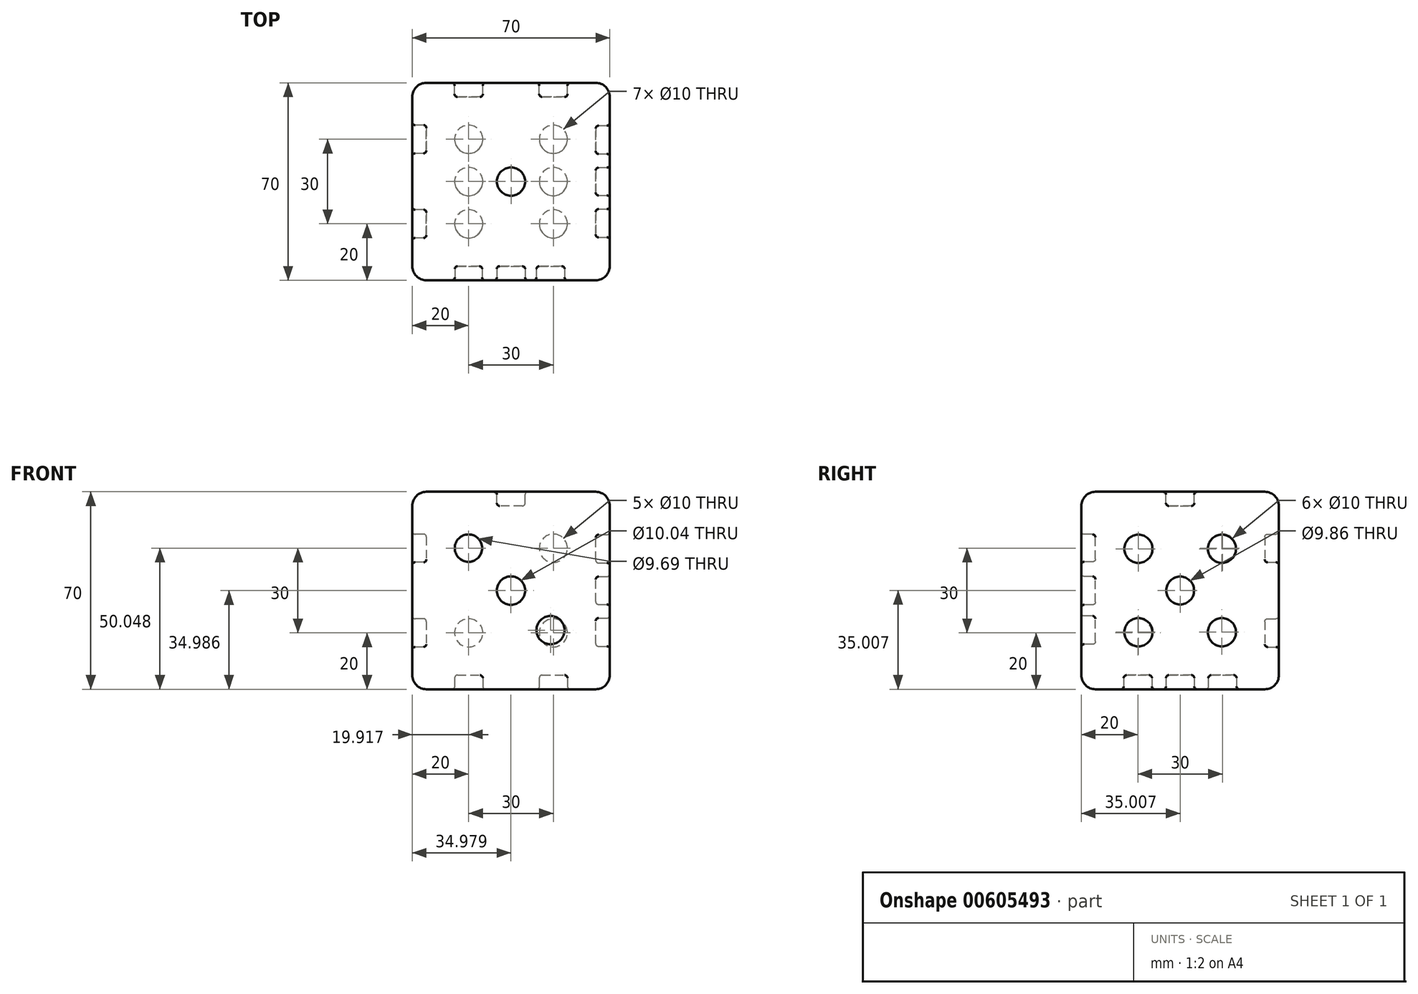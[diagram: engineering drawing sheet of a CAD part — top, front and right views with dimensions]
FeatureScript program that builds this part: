
annotation { "Feature Type Name" : "Feature", "Feature Type Description" : "" }
export const myFeature = defineFeature(function(context is Context, id is Id, definition is map)
    precondition{}
    {
        {
            var Q0;
            Q0=qCreatedBy(makeId("Top.planeOp"),FACE);
            var sketch = newSketch(context, id + "F0", { "sketchPlane" : qUnion([Q0])});
            skLineSegment(sketch, "E0.bottom", {"start": v(-35, -35) * mm, "end": v(35, -35) * mm});
            skLineSegment(sketch, "E0.top", {"start": v(-35, 35) * mm, "end": v(35, 35) * mm});
            skLineSegment(sketch, "E0.left", {"start": v(-35, -35) * mm, "end": v(-35, 35) * mm});
            skLineSegment(sketch, "E0.right", {"start": v(35, -35) * mm, "end": v(35, 35) * mm});
            skPoint(sketch, "E0.middle", {"position": v(0, 0) * mm});
            skSolve(sketch);
        }
        {
            var Q0;
            Q0=makeQuery(id+"F0.imprint","IMPRINT",FACE,{"disambiguationData":[TD([[makeQuery(id+"F0.imprint","IMPRINT",EDGE,{"derivedFrom":sQuery(id+"F0.wireOp",EDGE,"E0.bottom")}),1.0]])]});
            extrude(context, id + "F1", {"entities" : qUnion([Q0]), "depth" : 70 * mm, "offsetDistance" : 25 * mm});
        }
        {
            var Q0;
            Q0=makeQuery(id+"F1.opExtrude","SWEPT_EDGE",EDGE,{"disambiguationData":[OSD([sQuery(id+"F0.wireOp",EDGE,"E0.bottom"),sQuery(id+"F0.wireOp",EDGE,"E0.left")])]});
            var Q1;
            Q1=makeQuery(id+"F1.opExtrude","SWEPT_FACE",FACE,{"disambiguationData":[OSD([sQuery(id+"F0.wireOp",EDGE,"E0.bottom")])]});
            var Q2;
            Q2=makeQuery(id+"F1.opExtrude","SWEPT_EDGE",EDGE,{"disambiguationData":[OSD([sQuery(id+"F0.wireOp",EDGE,"E0.bottom"),sQuery(id+"F0.wireOp",EDGE,"E0.right")])]});
            var Q3;
            Q3=makeQuery(id+"F1.opExtrude","CAP_FACE",FACE,{"disambiguationData":[OSD([sQuery(id+"F0.wireOp",EDGE,"E0.bottom"),sQuery(id+"F0.wireOp",EDGE,"E0.top"),sQuery(id+"F0.wireOp",EDGE,"E0.left"),sQuery(id+"F0.wireOp",EDGE,"E0.right")])],"isStart":false});
            var Q4;
            Q4=makeQuery(id+"F1.opExtrude","SWEPT_EDGE",EDGE,{"disambiguationData":[OSD([sQuery(id+"F0.wireOp",EDGE,"E0.top"),sQuery(id+"F0.wireOp",EDGE,"E0.right")])]});
            var Q5;
            Q5=makeQuery(id+"F1.opExtrude","CAP_EDGE",EDGE,{"disambiguationData":[OSD([sQuery(id+"F0.wireOp",EDGE,"E0.bottom")])],"isStart":true});
            var Q6;
            Q6=makeQuery(id+"F1.opExtrude","SWEPT_FACE",FACE,{"disambiguationData":[OSD([sQuery(id+"F0.wireOp",EDGE,"E0.left")])]});
            var Q7;
            Q7=makeQuery(id+"F1.opExtrude","CAP_EDGE",EDGE,{"disambiguationData":[OSD([sQuery(id+"F0.wireOp",EDGE,"E0.bottom")])],"isStart":false});
            var Q8;
            Q8=makeQuery(id+"F1.opExtrude","SWEPT_FACE",FACE,{"disambiguationData":[OSD([sQuery(id+"F0.wireOp",EDGE,"E0.right")])]});
            var Q9;
            Q9=makeQuery(id+"F1.opExtrude","CAP_EDGE",EDGE,{"disambiguationData":[OSD([sQuery(id+"F0.wireOp",EDGE,"E0.top")])],"isStart":false});
            var Q10;
            Q10=makeQuery(id+"F1.opExtrude","CAP_EDGE",EDGE,{"disambiguationData":[OSD([sQuery(id+"F0.wireOp",EDGE,"E0.left")])],"isStart":false});
            var Q11;
            Q11=makeQuery(id+"F1.opExtrude","CAP_EDGE",EDGE,{"disambiguationData":[OSD([sQuery(id+"F0.wireOp",EDGE,"E0.right")])],"isStart":true});
            var Q12;
            Q12=makeQuery(id+"F1.opExtrude","CAP_EDGE",EDGE,{"disambiguationData":[OSD([sQuery(id+"F0.wireOp",EDGE,"E0.right")])],"isStart":false});
            var Q13;
            Q13=makeQuery(id+"F1.opExtrude","CAP_FACE",FACE,{"disambiguationData":[OSD([sQuery(id+"F0.wireOp",EDGE,"E0.bottom"),sQuery(id+"F0.wireOp",EDGE,"E0.top"),sQuery(id+"F0.wireOp",EDGE,"E0.left"),sQuery(id+"F0.wireOp",EDGE,"E0.right")])],"isStart":true});
            var Q14;
            Q14=makeQuery(id+"F1.opExtrude","SWEPT_EDGE",EDGE,{"disambiguationData":[OSD([sQuery(id+"F0.wireOp",EDGE,"E0.top"),sQuery(id+"F0.wireOp",EDGE,"E0.left")])]});
            var Q15;
            Q15=makeQuery(id+"F1.opExtrude","SWEPT_FACE",FACE,{"disambiguationData":[OSD([sQuery(id+"F0.wireOp",EDGE,"E0.top")])]});
            var Q16;
            Q16=makeQuery(id+"F1.opExtrude","CAP_EDGE",EDGE,{"disambiguationData":[OSD([sQuery(id+"F0.wireOp",EDGE,"E0.top")])],"isStart":true});
            var Q17;
            Q17=makeQuery(id+"F1.opExtrude","CAP_EDGE",EDGE,{"disambiguationData":[OSD([sQuery(id+"F0.wireOp",EDGE,"E0.left")])],"isStart":true});
            fillet(context, id + "F2", {"entities" : qUnion([Q0, Q1, Q2, Q3, Q4, Q5, Q6, Q7, Q8, Q9, Q10, Q11, Q12, Q13, Q14, Q15, Q16, Q17]), "radius" : 5 * mm, "tangentPropagation" : true, "allowEdgeOverflow" : false});
        }
        {
            var Q0;
            Q0=makeQuery(id+"F1.opExtrude","CAP_FACE",FACE,{"disambiguationData":[OSD([sQuery(id+"F0.wireOp",EDGE,"E0.bottom"),sQuery(id+"F0.wireOp",EDGE,"E0.top"),sQuery(id+"F0.wireOp",EDGE,"E0.left"),sQuery(id+"F0.wireOp",EDGE,"E0.right")])],"isStart":false});
            var sketch = newSketch(context, id + "F3", { "sketchPlane" : qUnion([Q0])});
            skCircle(sketch, "E1", {"center": v(0, 0) * mm, "radius": 5 * mm});
            skSolve(sketch);
        }
        {
            var Q0;
            Q0=makeQuery(id+"F3.imprint","IMPRINT",FACE,{"disambiguationData":[TD([[makeQuery(id+"F3.imprint","IMPRINT",EDGE,{"derivedFrom":sQuery(id+"F3.wireOp",EDGE,"E1")}),1.0]])]});
            extrude(context, id + "F4", {"entities" : qUnion([Q0]), "operationType" : NewBodyOperationType.REMOVE, "oppositeDirection" : true, "depth" : 5 * mm, "offsetDistance" : 25 * mm});
        }
        {
            var Q0;
            Q0=makeQuery(id+"F1.opExtrude","SWEPT_FACE",FACE,{"disambiguationData":[OSD([sQuery(id+"F0.wireOp",EDGE,"E0.bottom")])]});
            var sketch = newSketch(context, id + "F5", { "sketchPlane" : qUnion([Q0])});
            skCircle(sketch, "E2", {"center": v(-0.02, 34.99) * mm, "radius": 5.02 * mm});
            skCircle(sketch, "E3", {"center": v(-15.08, 50.05) * mm, "radius": 4.85 * mm});
            skCircle(sketch, "E4", {"center": v(14, 20.97) * mm, "radius": 5 * mm});
            skSolve(sketch);
        }
        {
            var Q0;
            Q0=makeQuery(id+"F5.imprint","IMPRINT",FACE,{"disambiguationData":[TD([[makeQuery(id+"F5.imprint","IMPRINT",EDGE,{"derivedFrom":sQuery(id+"F5.wireOp",EDGE,"E3")}),1.0]])]});
            var Q1;
            Q1=makeQuery(id+"F5.imprint","IMPRINT",FACE,{"disambiguationData":[TD([[makeQuery(id+"F5.imprint","IMPRINT",EDGE,{"derivedFrom":sQuery(id+"F5.wireOp",EDGE,"E2")}),1.0]])]});
            var Q2;
            Q2=makeQuery(id+"F5.imprint","IMPRINT",FACE,{"disambiguationData":[TD([[makeQuery(id+"F5.imprint","IMPRINT",EDGE,{"derivedFrom":sQuery(id+"F5.wireOp",EDGE,"E4")}),1.0]])]});
            extrude(context, id + "F6", {"entities" : qUnion([Q0, Q1, Q2]), "operationType" : NewBodyOperationType.REMOVE, "oppositeDirection" : true, "depth" : 5 * mm, "offsetDistance" : 25 * mm});
        }
        {
            var Q0;
            Q0=makeQuery(id+"F1.opExtrude","SWEPT_FACE",FACE,{"disambiguationData":[OSD([sQuery(id+"F0.wireOp",EDGE,"E0.top")])]});
            var sketch = newSketch(context, id + "F7", { "sketchPlane" : qUnion([Q0])});
            skCircle(sketch, "E5", {"center": v(-15, 50) * mm, "radius": 5 * mm});
            skCircle(sketch, "E6", {"center": v(-15, 20) * mm, "radius": 5 * mm});
            skCircle(sketch, "E7", {"center": v(15, 50) * mm, "radius": 5 * mm});
            skCircle(sketch, "E8", {"center": v(15, 20) * mm, "radius": 5 * mm});
            skSolve(sketch);
        }
        {
            var Q0;
            Q0=makeQuery(id+"F7.imprint","IMPRINT",FACE,{"disambiguationData":[TD([[makeQuery(id+"F7.imprint","IMPRINT",EDGE,{"derivedFrom":sQuery(id+"F7.wireOp",EDGE,"E7")}),1.0]])]});
            var Q1;
            Q1=makeQuery(id+"F7.imprint","IMPRINT",FACE,{"disambiguationData":[TD([[makeQuery(id+"F7.imprint","IMPRINT",EDGE,{"derivedFrom":sQuery(id+"F7.wireOp",EDGE,"E8")}),1.0]])]});
            var Q2;
            Q2=makeQuery(id+"F7.imprint","IMPRINT",FACE,{"disambiguationData":[TD([[makeQuery(id+"F7.imprint","IMPRINT",EDGE,{"derivedFrom":sQuery(id+"F7.wireOp",EDGE,"E5")}),1.0]])]});
            var Q3;
            Q3=makeQuery(id+"F7.imprint","IMPRINT",FACE,{"disambiguationData":[TD([[makeQuery(id+"F7.imprint","IMPRINT",EDGE,{"derivedFrom":sQuery(id+"F7.wireOp",EDGE,"E6")}),1.0]])]});
            extrude(context, id + "F8", {"entities" : qUnion([Q0, Q1, Q2, Q3]), "operationType" : NewBodyOperationType.REMOVE, "oppositeDirection" : true, "depth" : 5 * mm, "offsetDistance" : 25 * mm});
        }
        {
            var Q0;
            Q0=makeQuery(id+"F1.opExtrude","CAP_FACE",FACE,{"disambiguationData":[OSD([sQuery(id+"F0.wireOp",EDGE,"E0.bottom"),sQuery(id+"F0.wireOp",EDGE,"E0.top"),sQuery(id+"F0.wireOp",EDGE,"E0.left"),sQuery(id+"F0.wireOp",EDGE,"E0.right")])],"isStart":true});
            var sketch = newSketch(context, id + "F9", { "sketchPlane" : qUnion([Q0])});
            skCircle(sketch, "E9", {"center": v(-15, 0) * mm, "radius": 5 * mm});
            skCircle(sketch, "E10", {"center": v(15, 0) * mm, "radius": 5 * mm});
            skCircle(sketch, "E11", {"center": v(-15, 15) * mm, "radius": 5 * mm});
            skCircle(sketch, "E12", {"center": v(15, 15) * mm, "radius": 5 * mm});
            skCircle(sketch, "E13", {"center": v(15, -15) * mm, "radius": 5 * mm});
            skCircle(sketch, "E14", {"center": v(-15, -15) * mm, "radius": 5 * mm});
            skSolve(sketch);
        }
        {
            var Q0;
            Q0=makeQuery(id+"F9.imprint","IMPRINT",FACE,{"disambiguationData":[TD([[makeQuery(id+"F9.imprint","IMPRINT",EDGE,{"derivedFrom":sQuery(id+"F9.wireOp",EDGE,"E11")}),1.0]])]});
            var Q1;
            Q1=makeQuery(id+"F9.imprint","IMPRINT",FACE,{"disambiguationData":[TD([[makeQuery(id+"F9.imprint","IMPRINT",EDGE,{"derivedFrom":sQuery(id+"F9.wireOp",EDGE,"E10")}),1.0]])]});
            var Q2;
            Q2=makeQuery(id+"F9.imprint","IMPRINT",FACE,{"disambiguationData":[TD([[makeQuery(id+"F9.imprint","IMPRINT",EDGE,{"derivedFrom":sQuery(id+"F9.wireOp",EDGE,"E9")}),1.0]])]});
            var Q3;
            Q3=makeQuery(id+"F9.imprint","IMPRINT",FACE,{"disambiguationData":[TD([[makeQuery(id+"F9.imprint","IMPRINT",EDGE,{"derivedFrom":sQuery(id+"F9.wireOp",EDGE,"E14")}),1.0]])]});
            var Q4;
            Q4=makeQuery(id+"F9.imprint","IMPRINT",FACE,{"disambiguationData":[TD([[makeQuery(id+"F9.imprint","IMPRINT",EDGE,{"derivedFrom":sQuery(id+"F9.wireOp",EDGE,"E13")}),1.0]])]});
            var Q5;
            Q5=makeQuery(id+"F9.imprint","IMPRINT",FACE,{"disambiguationData":[TD([[makeQuery(id+"F9.imprint","IMPRINT",EDGE,{"derivedFrom":sQuery(id+"F9.wireOp",EDGE,"E12")}),1.0]])]});
            extrude(context, id + "F10", {"entities" : qUnion([Q0, Q1, Q2, Q3, Q4, Q5]), "operationType" : NewBodyOperationType.REMOVE, "oppositeDirection" : true, "depth" : 5 * mm, "offsetDistance" : 25 * mm});
        }
        {
            var Q0;
            Q0=makeQuery(id+"F1.opExtrude","SWEPT_FACE",FACE,{"disambiguationData":[OSD([sQuery(id+"F0.wireOp",EDGE,"E0.right")])]});
            var sketch = newSketch(context, id + "F11", { "sketchPlane" : qUnion([Q0])});
            skCircle(sketch, "E15", {"center": v(0, 35) * mm, "radius": 4.93 * mm});
            skCircle(sketch, "E16", {"center": v(-14.78, 49.8) * mm, "radius": 5 * mm});
            skCircle(sketch, "E17", {"center": v(14.8, 49.8) * mm, "radius": 5 * mm});
            skCircle(sketch, "E18", {"center": v(14.8, 20.22) * mm, "radius": 5 * mm});
            skCircle(sketch, "E19", {"center": v(-14.78, 20.22) * mm, "radius": 5 * mm});
            skSolve(sketch);
        }
        {
            var Q0;
            Q0=makeQuery(id+"F11.imprint","IMPRINT",FACE,{"disambiguationData":[TD([[makeQuery(id+"F11.imprint","IMPRINT",EDGE,{"derivedFrom":sQuery(id+"F11.wireOp",EDGE,"E16")}),1.0]])]});
            var Q1;
            Q1=makeQuery(id+"F11.imprint","IMPRINT",FACE,{"disambiguationData":[TD([[makeQuery(id+"F11.imprint","IMPRINT",EDGE,{"derivedFrom":sQuery(id+"F11.wireOp",EDGE,"E19")}),1.0]])]});
            var Q2;
            Q2=makeQuery(id+"F11.imprint","IMPRINT",FACE,{"disambiguationData":[TD([[makeQuery(id+"F11.imprint","IMPRINT",EDGE,{"derivedFrom":sQuery(id+"F11.wireOp",EDGE,"E15")}),1.0]])]});
            var Q3;
            Q3=makeQuery(id+"F11.imprint","IMPRINT",FACE,{"disambiguationData":[TD([[makeQuery(id+"F11.imprint","IMPRINT",EDGE,{"derivedFrom":sQuery(id+"F11.wireOp",EDGE,"E17")}),1.0]])]});
            var Q4;
            Q4=makeQuery(id+"F11.imprint","IMPRINT",FACE,{"disambiguationData":[TD([[makeQuery(id+"F11.imprint","IMPRINT",EDGE,{"derivedFrom":sQuery(id+"F11.wireOp",EDGE,"E18")}),1.0]])]});
            extrude(context, id + "F12", {"entities" : qUnion([Q0, Q1, Q2, Q3, Q4]), "operationType" : NewBodyOperationType.REMOVE, "oppositeDirection" : true, "depth" : 5 * mm, "offsetDistance" : 25 * mm});
        }
        {
            var Q0;
            Q0=makeQuery(id+"F1.opExtrude","SWEPT_FACE",FACE,{"disambiguationData":[OSD([sQuery(id+"F0.wireOp",EDGE,"E0.left")])]});
            var sketch = newSketch(context, id + "F13", { "sketchPlane" : qUnion([Q0])});
            skCircle(sketch, "E20", {"center": v(-15, 50) * mm, "radius": 5 * mm});
            skCircle(sketch, "E21", {"center": v(15, 20) * mm, "radius": 5 * mm});
            skSolve(sketch);
        }
        {
            var Q0;
            Q0=makeQuery(id+"F4.boolean.opBoolean","COPY",FACE,{"derivedFrom":makeQuery(id+"F4.opExtrude","SWEPT_FACE",FACE,{"disambiguationData":[OSD([sQuery(id+"F3.wireOp",EDGE,"E1")])]})});
            fillet(context, id + "F14", {"entities" : qUnion([Q0]), "radius" : 1 * mm, "tangentPropagation" : true, "allowEdgeOverflow" : false});
        }
        {
            var Q0;
            Q0=makeQuery(id+"F6.boolean.opBoolean","COPY",FACE,{"derivedFrom":makeQuery(id+"F6.opExtrude","SWEPT_FACE",FACE,{"disambiguationData":[OSD([sQuery(id+"F5.wireOp",EDGE,"E3")])]})});
            var Q1;
            Q1=makeQuery(id+"F6.boolean.opBoolean","COPY",FACE,{"derivedFrom":makeQuery(id+"F6.opExtrude","SWEPT_FACE",FACE,{"disambiguationData":[OSD([sQuery(id+"F5.wireOp",EDGE,"E4")])]})});
            var Q2;
            Q2=makeQuery(id+"F6.boolean.opBoolean","COPY",FACE,{"derivedFrom":makeQuery(id+"F6.opExtrude","SWEPT_FACE",FACE,{"disambiguationData":[OSD([sQuery(id+"F5.wireOp",EDGE,"E2")])]})});
            fillet(context, id + "F15", {"entities" : qUnion([Q0, Q1, Q2]), "radius" : 1 * mm, "tangentPropagation" : true, "allowEdgeOverflow" : false});
        }
        {
            var Q0;
            Q0=makeQuery(id+"F12.boolean.opBoolean","COPY",FACE,{"derivedFrom":makeQuery(id+"F12.opExtrude","SWEPT_FACE",FACE,{"disambiguationData":[OSD([sQuery(id+"F11.wireOp",EDGE,"E16")])]})});
            var Q1;
            Q1=makeQuery(id+"F12.boolean.opBoolean","COPY",FACE,{"derivedFrom":makeQuery(id+"F12.opExtrude","SWEPT_FACE",FACE,{"disambiguationData":[OSD([sQuery(id+"F11.wireOp",EDGE,"E17")])]})});
            var Q2;
            Q2=makeQuery(id+"F12.boolean.opBoolean","COPY",FACE,{"derivedFrom":makeQuery(id+"F12.opExtrude","SWEPT_FACE",FACE,{"disambiguationData":[OSD([sQuery(id+"F11.wireOp",EDGE,"E18")])]})});
            var Q3;
            Q3=makeQuery(id+"F12.boolean.opBoolean","COPY",FACE,{"derivedFrom":makeQuery(id+"F12.opExtrude","SWEPT_FACE",FACE,{"disambiguationData":[OSD([sQuery(id+"F11.wireOp",EDGE,"E15")])]})});
            var Q4;
            Q4=makeQuery(id+"F12.boolean.opBoolean","COPY",FACE,{"derivedFrom":makeQuery(id+"F12.opExtrude","SWEPT_FACE",FACE,{"disambiguationData":[OSD([sQuery(id+"F11.wireOp",EDGE,"E19")])]})});
            fillet(context, id + "F16", {"entities" : qUnion([Q0, Q1, Q2, Q3, Q4]), "radius" : 1 * mm, "tangentPropagation" : true, "allowEdgeOverflow" : false});
        }
        {
            var Q0;
            Q0=makeQuery(id+"F13.imprint","IMPRINT",FACE,{"disambiguationData":[TD([[makeQuery(id+"F13.imprint","IMPRINT",EDGE,{"derivedFrom":sQuery(id+"F13.wireOp",EDGE,"E20")}),1.0]])]});
            var Q1;
            Q1=makeQuery(id+"F13.imprint","IMPRINT",FACE,{"disambiguationData":[TD([[makeQuery(id+"F13.imprint","IMPRINT",EDGE,{"derivedFrom":sQuery(id+"F13.wireOp",EDGE,"E21")}),1.0]])]});
            extrude(context, id + "F17", {"entities" : qUnion([Q0, Q1]), "operationType" : NewBodyOperationType.REMOVE, "oppositeDirection" : true, "depth" : 5 * mm, "offsetDistance" : 25 * mm});
        }
        {
            var Q0;
            Q0=makeQuery(id+"F17.boolean.opBoolean","COPY",FACE,{"derivedFrom":makeQuery(id+"F17.opExtrude","SWEPT_FACE",FACE,{"disambiguationData":[OSD([sQuery(id+"F13.wireOp",EDGE,"E20")])]})});
            var Q1;
            Q1=makeQuery(id+"F17.boolean.opBoolean","COPY",FACE,{"derivedFrom":makeQuery(id+"F17.opExtrude","SWEPT_FACE",FACE,{"disambiguationData":[OSD([sQuery(id+"F13.wireOp",EDGE,"E21")])]})});
            fillet(context, id + "F18", {"entities" : qUnion([Q0, Q1]), "radius" : 1 * mm, "tangentPropagation" : true, "allowEdgeOverflow" : false});
        }
        {
            var Q0;
            Q0=makeQuery(id+"F10.boolean.opBoolean","COPY",FACE,{"derivedFrom":makeQuery(id+"F10.opExtrude","SWEPT_FACE",FACE,{"disambiguationData":[OSD([sQuery(id+"F9.wireOp",EDGE,"E12")])]})});
            var Q1;
            Q1=makeQuery(id+"F10.boolean.opBoolean","COPY",FACE,{"derivedFrom":makeQuery(id+"F10.opExtrude","SWEPT_FACE",FACE,{"disambiguationData":[OSD([sQuery(id+"F9.wireOp",EDGE,"E10")])]})});
            var Q2;
            Q2=makeQuery(id+"F10.boolean.opBoolean","COPY",FACE,{"derivedFrom":makeQuery(id+"F10.opExtrude","SWEPT_FACE",FACE,{"disambiguationData":[OSD([sQuery(id+"F9.wireOp",EDGE,"E13")])]})});
            var Q3;
            Q3=makeQuery(id+"F10.boolean.opBoolean","COPY",FACE,{"derivedFrom":makeQuery(id+"F10.opExtrude","SWEPT_FACE",FACE,{"disambiguationData":[OSD([sQuery(id+"F9.wireOp",EDGE,"E14")])]})});
            var Q4;
            Q4=makeQuery(id+"F10.boolean.opBoolean","COPY",FACE,{"derivedFrom":makeQuery(id+"F10.opExtrude","SWEPT_FACE",FACE,{"disambiguationData":[OSD([sQuery(id+"F9.wireOp",EDGE,"E9")])]})});
            var Q5;
            Q5=makeQuery(id+"F10.boolean.opBoolean","COPY",FACE,{"derivedFrom":makeQuery(id+"F10.opExtrude","SWEPT_FACE",FACE,{"disambiguationData":[OSD([sQuery(id+"F9.wireOp",EDGE,"E11")])]})});
            fillet(context, id + "F19", {"entities" : qUnion([Q0, Q1, Q2, Q3, Q4, Q5]), "radius" : 1 * mm, "tangentPropagation" : true, "allowEdgeOverflow" : false});
        }
        {
            var Q0;
            Q0=makeQuery(id+"F8.boolean.opBoolean","COPY",FACE,{"derivedFrom":makeQuery(id+"F8.opExtrude","SWEPT_FACE",FACE,{"disambiguationData":[OSD([sQuery(id+"F7.wireOp",EDGE,"E5")])]})});
            var Q1;
            Q1=makeQuery(id+"F8.boolean.opBoolean","COPY",FACE,{"derivedFrom":makeQuery(id+"F8.opExtrude","SWEPT_FACE",FACE,{"disambiguationData":[OSD([sQuery(id+"F7.wireOp",EDGE,"E7")])]})});
            var Q2;
            Q2=makeQuery(id+"F8.boolean.opBoolean","COPY",FACE,{"derivedFrom":makeQuery(id+"F8.opExtrude","SWEPT_FACE",FACE,{"disambiguationData":[OSD([sQuery(id+"F7.wireOp",EDGE,"E8")])]})});
            var Q3;
            Q3=makeQuery(id+"F8.boolean.opBoolean","COPY",FACE,{"derivedFrom":makeQuery(id+"F8.opExtrude","SWEPT_FACE",FACE,{"disambiguationData":[OSD([sQuery(id+"F7.wireOp",EDGE,"E6")])]})});
            fillet(context, id + "F20", {"entities" : qUnion([Q0, Q1, Q2, Q3]), "radius" : 1 * mm, "tangentPropagation" : true, "allowEdgeOverflow" : false});
        }
    });
